# Revit family: Sanitary_Showers_hansgrohe_25031XXX-Rainfinity-Digital-Overhead-sho_NEW
name_source: partatom
category: Plumbing Fixtures
revit_build: Autodesk Revit 2015 (Build: 20140903_1530(x64)
units: mm (PartAtom-declared; Revit-internal decimal feet)

## types (2) — shared parameters
Always visible = Yes
BIMobject category = Showers
BIMobject category code = sanitary-showers
BIMobject main category = Sanitary
BIMobject main category code = sanitary
Brand url = http://www.hansgrohe-int.com
Design country = Germany
Edition number = 1
GTIN code = https://4059625269084
IFC Classification = Sanitary Terminal
Installation instructions = https://www.hansgrohe.de
Manufacturer country = Germany
Manufacturer name = hansgrohe
Material 2 = Hansgrohe - Rainfinity Digital - Graphite
Product Guid = d6336d44-b19e-4cd2-978e-28a9e64ef17c
Product SKU = 25031XXX
Product data url = https://bimobject.com
Product name = 25031XXX Rainfinity Digital Overhead shower 360 1jet with ceiling connection
Product url = https://www.hansgrohe.de
QR code = http://bimobject.com
Technical description = https://www.hansgrohe.de

## per-type parameters (varying)
| type | Material 1 |
| 700 Matt White | Hansgrohe - Rainfinity Digital - 700 Matt White |
| 000 Chrome | Hansgrohe - Rainfinity Digital - 000 Chrome |

## geometry (parser evidence)
native form markers: Sweep x4
no freeform markers — native parametric forms only
